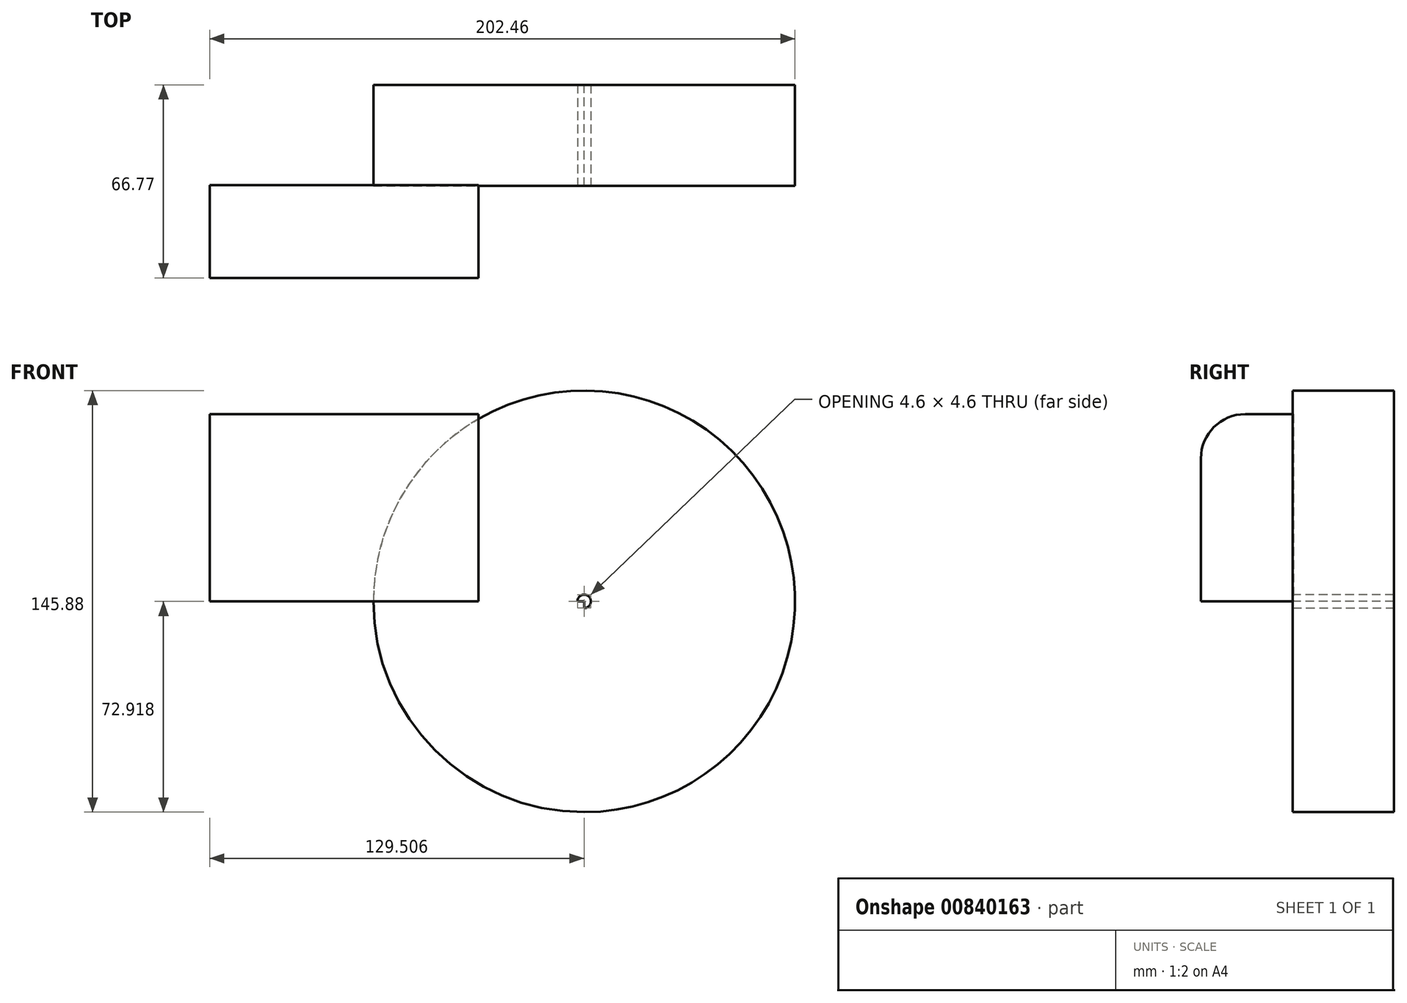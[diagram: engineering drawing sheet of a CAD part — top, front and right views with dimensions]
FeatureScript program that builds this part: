
annotation { "Feature Type Name" : "Feature", "Feature Type Description" : "" }
export const myFeature = defineFeature(function(context is Context, id is Id, definition is map)
    precondition{}
    {
        {
            var Q0;
            Q0=qCreatedBy(makeId("Top.planeOp"),FACE);
            var sketch = newSketch(context, id + "F0", { "sketchPlane" : qUnion([Q0])});
            skLineSegment(sketch, "E0.bottom", {"start": v(-56.63, 15.56) * mm, "end": v(36.4, 15.56) * mm});
            skLineSegment(sketch, "E0.top", {"start": v(-56.63, -16.49) * mm, "end": v(36.4, -16.49) * mm});
            skLineSegment(sketch, "E0.left", {"start": v(-56.63, 15.56) * mm, "end": v(-56.63, -16.49) * mm});
            skLineSegment(sketch, "E0.right", {"start": v(36.4, 15.56) * mm, "end": v(36.4, -16.49) * mm});
            skSolve(sketch);
        }
        {
            var Q0;
            Q0 = qSketchRegion(id + "F0", true);
            extrude(context, id + "F1", {"entities" : qUnion([Q0]), "depth" : 64.77 * mm, "offsetDistance" : 25.4 * mm});
        }
        {
            var Q0;
            Q0=makeQuery(id+"F1.opExtrude","CAP_EDGE",EDGE,{"disambiguationData":[OSD([sQuery(id+"F0.wireOp",EDGE,"E0.top")])],"isStart":false});
            fillet(context, id + "F2", {"entities" : qUnion([Q0]), "radius" : 15.33 * mm, "tangentPropagation" : true, "allowEdgeOverflow" : false});
        }
        {
            var Q0;
            Q0=qCreatedBy(makeId("Right.planeOp"),FACE);
            var sketch = newSketch(context, id + "F3", { "sketchPlane" : qUnion([Q0])});
            skLineSegment(sketch, "E1.bottom", {"start": v(15.3, -2.32) * mm, "end": v(50.28, -2.32) * mm});
            skLineSegment(sketch, "E1.top", {"start": v(15.3, 0) * mm, "end": v(50.28, 0) * mm});
            skLineSegment(sketch, "E1.left", {"start": v(15.3, -2.32) * mm, "end": v(15.3, 0) * mm});
            skLineSegment(sketch, "E1.right", {"start": v(50.28, -2.32) * mm, "end": v(50.28, 0) * mm});
            skSolve(sketch);
        }
        {
            var Q0;
            Q0 = qSketchRegion(id + "F3", true);
            extrude(context, id + "F4", {"entities" : qUnion([Q0]), "operationType" : NewBodyOperationType.ADD, "depth" : 72.9 * mm, "offsetDistance" : 25.4 * mm});
        }
        {
            var Q0;
            Q0=makeQuery(id+"F4.opExtrude","SWEPT_FACE",FACE,{"disambiguationData":[OSD([sQuery(id+"F3.wireOp",EDGE,"E1.bottom")])]});
            var Q1;
            Q1=makeQuery(id+"F4.opExtrude","CAP_EDGE",EDGE,{"disambiguationData":[OSD([sQuery(id+"F3.wireOp",EDGE,"E1.top")])],"isStart":false});
            revolve(context, id + "F5", {"operationType" : NewBodyOperationType.ADD, "surfaceOperationType" : NewSurfaceOperationType.NEW, "entities" : qUnion([Q0]), "axis" : qUnion([Q1]), "revolveType" : RevolveType.FULL});
        }
    });
